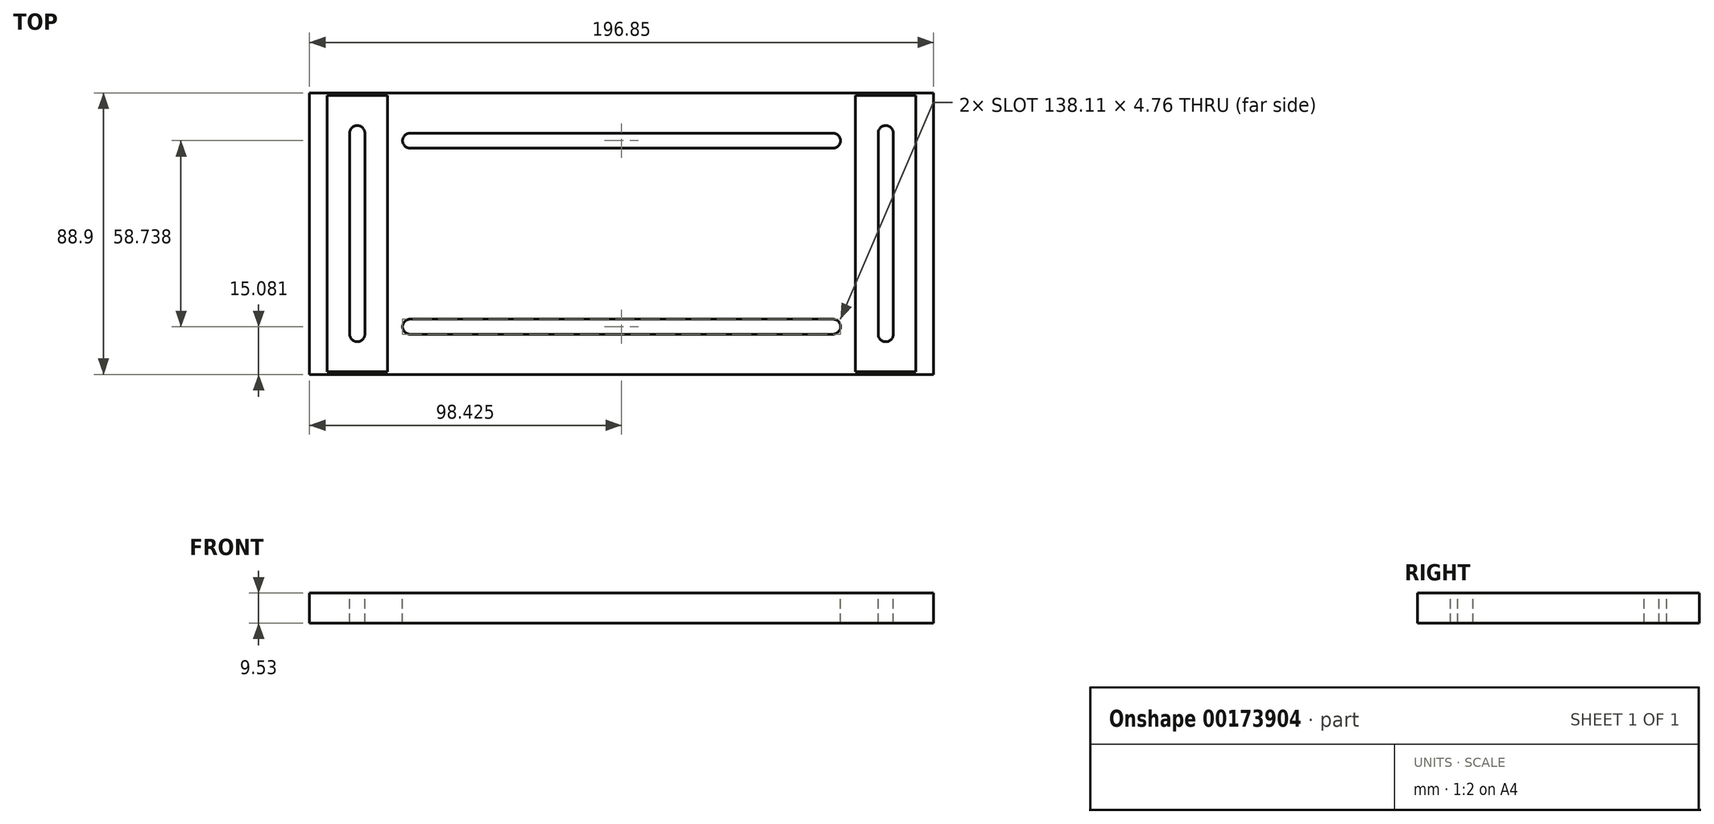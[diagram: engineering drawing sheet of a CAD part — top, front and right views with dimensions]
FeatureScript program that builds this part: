
annotation { "Feature Type Name" : "Feature", "Feature Type Description" : "" }
export const myFeature = defineFeature(function(context is Context, id is Id, definition is map)
    precondition{}
    {
        {
            var Q0;
            Q0=qCreatedBy(makeId("Top.planeOp"),FACE);
            var sketch = newSketch(context, id + "F0", { "sketchPlane" : qUnion([Q0])});
            skLineSegment(sketch, "E0.bottom", {"start": v(0, 0) * mm, "end": v(196.85, 0) * mm});
            skLineSegment(sketch, "E0.top", {"start": v(0, 88.9) * mm, "end": v(196.85, 88.9) * mm});
            skLineSegment(sketch, "E0.left", {"start": v(0, 0) * mm, "end": v(0, 88.9) * mm});
            skLineSegment(sketch, "E0.right", {"start": v(196.85, 0) * mm, "end": v(196.85, 88.9) * mm});
            skSolve(sketch);
        }
        {
            var Q0;
            Q0 = qSketchRegion(id + "F0", true);
            extrude(context, id + "F1", {"entities" : qUnion([Q0]), "depth" : 9.52 * mm});
        }
        {
            var Q0;
            Q0=makeQuery(id+"F1.opExtrude","CAP_FACE",FACE,{"disambiguationData":[OSD([sQuery(id+"F0.wireOp",EDGE,"E0.bottom"),sQuery(id+"F0.wireOp",EDGE,"E0.top"),sQuery(id+"F0.wireOp",EDGE,"E0.left"),sQuery(id+"F0.wireOp",EDGE,"E0.right")])],"isStart":false});
            var sketch = newSketch(context, id + "F2", { "sketchPlane" : qUnion([Q0])});
            skLineSegment(sketch, "E1.bottom", {"start": v(12.7, 12.7) * mm, "end": v(17.46, 12.7) * mm});
            skLineSegment(sketch, "E1.top", {"start": v(12.7, 76.2) * mm, "end": v(17.46, 76.2) * mm});
            skLineSegment(sketch, "E1.left", {"start": v(12.7, 12.7) * mm, "end": v(12.7, 76.2) * mm});
            skLineSegment(sketch, "E1.right", {"start": v(17.46, 12.7) * mm, "end": v(17.46, 76.2) * mm});
            skLineSegment(sketch, "E2.bottom", {"start": v(184.15, 12.7) * mm, "end": v(179.39, 12.7) * mm});
            skLineSegment(sketch, "E2.top", {"start": v(184.15, 76.2) * mm, "end": v(179.39, 76.2) * mm});
            skLineSegment(sketch, "E2.left", {"start": v(184.15, 12.7) * mm, "end": v(184.15, 76.2) * mm});
            skLineSegment(sketch, "E2.right", {"start": v(179.39, 12.7) * mm, "end": v(179.39, 76.2) * mm});
            skLineSegment(sketch, "E3.bottom", {"start": v(31.75, 76.2) * mm, "end": v(165.1, 76.2) * mm});
            skLineSegment(sketch, "E3.top", {"start": v(31.75, 71.44) * mm, "end": v(165.1, 71.44) * mm});
            skLineSegment(sketch, "E3.left", {"start": v(31.75, 76.2) * mm, "end": v(31.75, 71.44) * mm});
            skLineSegment(sketch, "E3.right", {"start": v(165.1, 76.2) * mm, "end": v(165.1, 71.44) * mm});
            skLineSegment(sketch, "E4.bottom", {"start": v(31.75, 17.46) * mm, "end": v(165.1, 17.46) * mm});
            skLineSegment(sketch, "E4.top", {"start": v(31.75, 12.7) * mm, "end": v(165.1, 12.7) * mm});
            skLineSegment(sketch, "E4.left", {"start": v(31.75, 17.46) * mm, "end": v(31.75, 12.7) * mm});
            skLineSegment(sketch, "E4.right", {"start": v(165.1, 17.46) * mm, "end": v(165.1, 12.7) * mm});
            skCircle(sketch, "E5", {"center": v(15.08, 76.2) * mm, "radius": 2.38 * mm});
            skCircle(sketch, "E6", {"center": v(31.75, 73.82) * mm, "radius": 2.38 * mm});
            skCircle(sketch, "E7", {"center": v(31.75, 15.08) * mm, "radius": 2.38 * mm});
            skCircle(sketch, "E8", {"center": v(181.77, 76.2) * mm, "radius": 2.38 * mm});
            skCircle(sketch, "E9", {"center": v(15.08, 12.7) * mm, "radius": 2.38 * mm});
            skCircle(sketch, "E10", {"center": v(165.1, 15.08) * mm, "radius": 2.38 * mm});
            skCircle(sketch, "E11", {"center": v(181.77, 12.7) * mm, "radius": 2.38 * mm});
            skCircle(sketch, "E12", {"center": v(165.1, 73.82) * mm, "radius": 2.38 * mm});
            skSolve(sketch);
        }
        {
            var Q0;
            Q0 = qSketchRegion(id + "F2", true);
            extrude(context, id + "F3", {"entities" : qUnion([Q0]), "operationType" : NewBodyOperationType.REMOVE, "oppositeDirection" : true, "depth" : 25.4 * mm});
        }
        {
            var Q0;
            Q0=makeQuery(id+"F1.opExtrude","CAP_FACE",FACE,{"disambiguationData":[OSD([sQuery(id+"F0.wireOp",EDGE,"E0.bottom"),sQuery(id+"F0.wireOp",EDGE,"E0.top"),sQuery(id+"F0.wireOp",EDGE,"E0.left"),sQuery(id+"F0.wireOp",EDGE,"E0.right")])],"isStart":false});
            var sketch = newSketch(context, id + "F4", { "sketchPlane" : qUnion([Q0])});
            skLineSegment(sketch, "E13.bottom", {"start": v(5.56, 88.1) * mm, "end": v(24.6, 88.1) * mm});
            skLineSegment(sketch, "E13.top", {"start": v(5.56, 0.8) * mm, "end": v(24.6, 0.8) * mm});
            skLineSegment(sketch, "E13.left", {"start": v(5.56, 88.1) * mm, "end": v(5.56, 0.8) * mm});
            skLineSegment(sketch, "E13.right", {"start": v(24.6, 88.1) * mm, "end": v(24.6, 0.8) * mm});
            skLineSegment(sketch, "E14.bottom", {"start": v(172.24, 88.1) * mm, "end": v(191.3, 88.1) * mm});
            skLineSegment(sketch, "E14.top", {"start": v(172.24, 0.8) * mm, "end": v(191.3, 0.8) * mm});
            skLineSegment(sketch, "E14.left", {"start": v(172.24, 88.1) * mm, "end": v(172.24, 0.8) * mm});
            skLineSegment(sketch, "E14.right", {"start": v(191.3, 88.1) * mm, "end": v(191.3, 0.8) * mm});
            skSolve(sketch);
        }
        {
            var Q0;
            Q0 = qSketchRegion(id + "F4", true);
            extrude(context, id + "F5", {"entities" : qUnion([Q0]), "operationType" : NewBodyOperationType.REMOVE, "oppositeDirection" : true, "depth" : 3 / 406.4 * mm});
        }
    });
